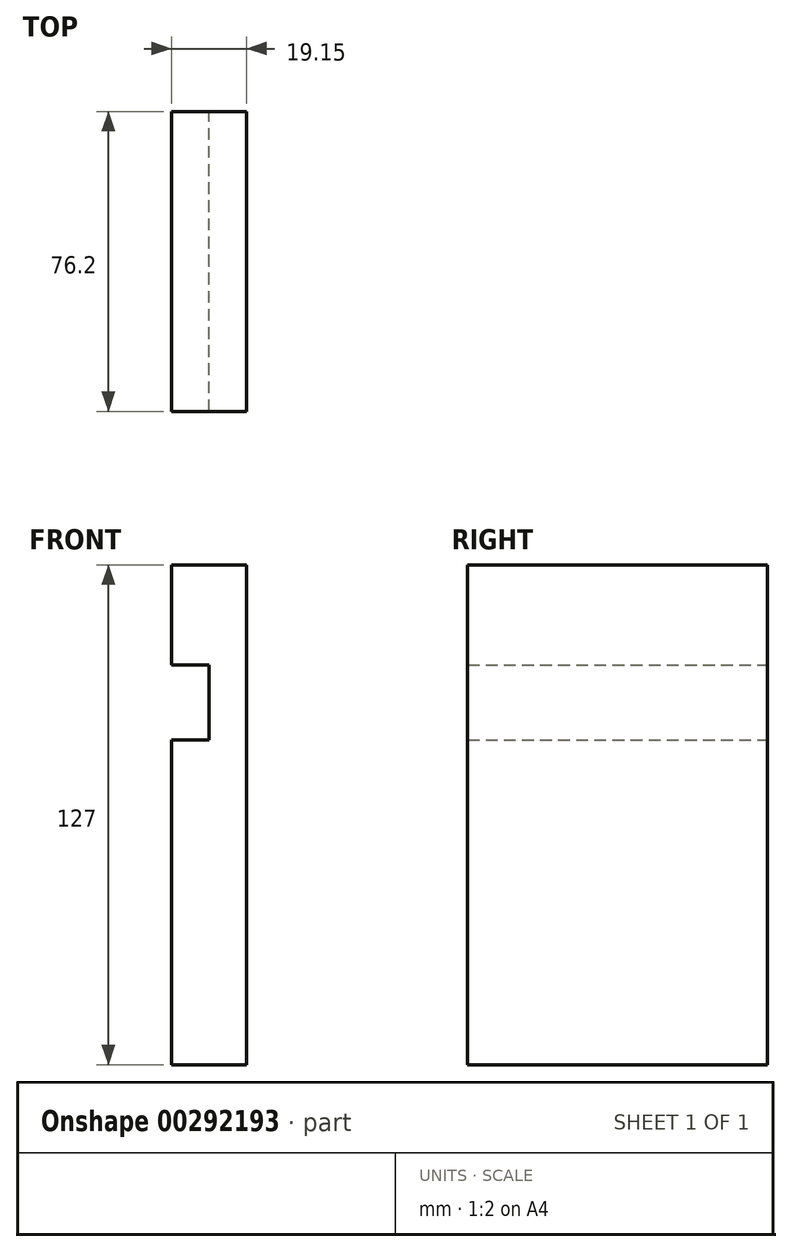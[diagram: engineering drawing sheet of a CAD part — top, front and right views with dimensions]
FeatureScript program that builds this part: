
annotation { "Feature Type Name" : "Feature", "Feature Type Description" : "" }
export const myFeature = defineFeature(function(context is Context, id is Id, definition is map)
    precondition{}
    {
        {
            var Q0;
            Q0=qCreatedBy(makeId("Front.planeOp"),FACE);
            var sketch = newSketch(context, id + "F0", { "sketchPlane" : qUnion([Q0])});
            skLineSegment(sketch, "E0", {"start": v(0, 0) * mm, "end": v(0, 127) * mm});
            skLineSegment(sketch, "E1", {"start": v(0, 127) * mm, "end": v(-19.05, 127) * mm});
            skLineSegment(sketch, "E2", {"start": v(-19.05, 127) * mm, "end": v(-19.05, 101.6) * mm});
            skLineSegment(sketch, "E3", {"start": v(-19.05, 101.6) * mm, "end": v(-9.52, 101.6) * mm});
            skLineSegment(sketch, "E4", {"start": v(-9.52, 101.6) * mm, "end": v(-9.52, 82.55) * mm});
            skLineSegment(sketch, "E5", {"start": v(-9.52, 82.55) * mm, "end": v(-19.15, 82.55) * mm});
            skLineSegment(sketch, "E6", {"start": v(-19.15, 82.55) * mm, "end": v(-19.15, 0) * mm});
            skLineSegment(sketch, "E7", {"start": v(-19.15, 0) * mm, "end": v(0, 0) * mm});
            skSolve(sketch);
        }
        {
            var Q0;
            Q0 = qSketchRegion(id + "F0", true);
            extrude(context, id + "F1", {"entities" : qUnion([Q0]), "depth" : 76.2 * mm});
        }
    });
